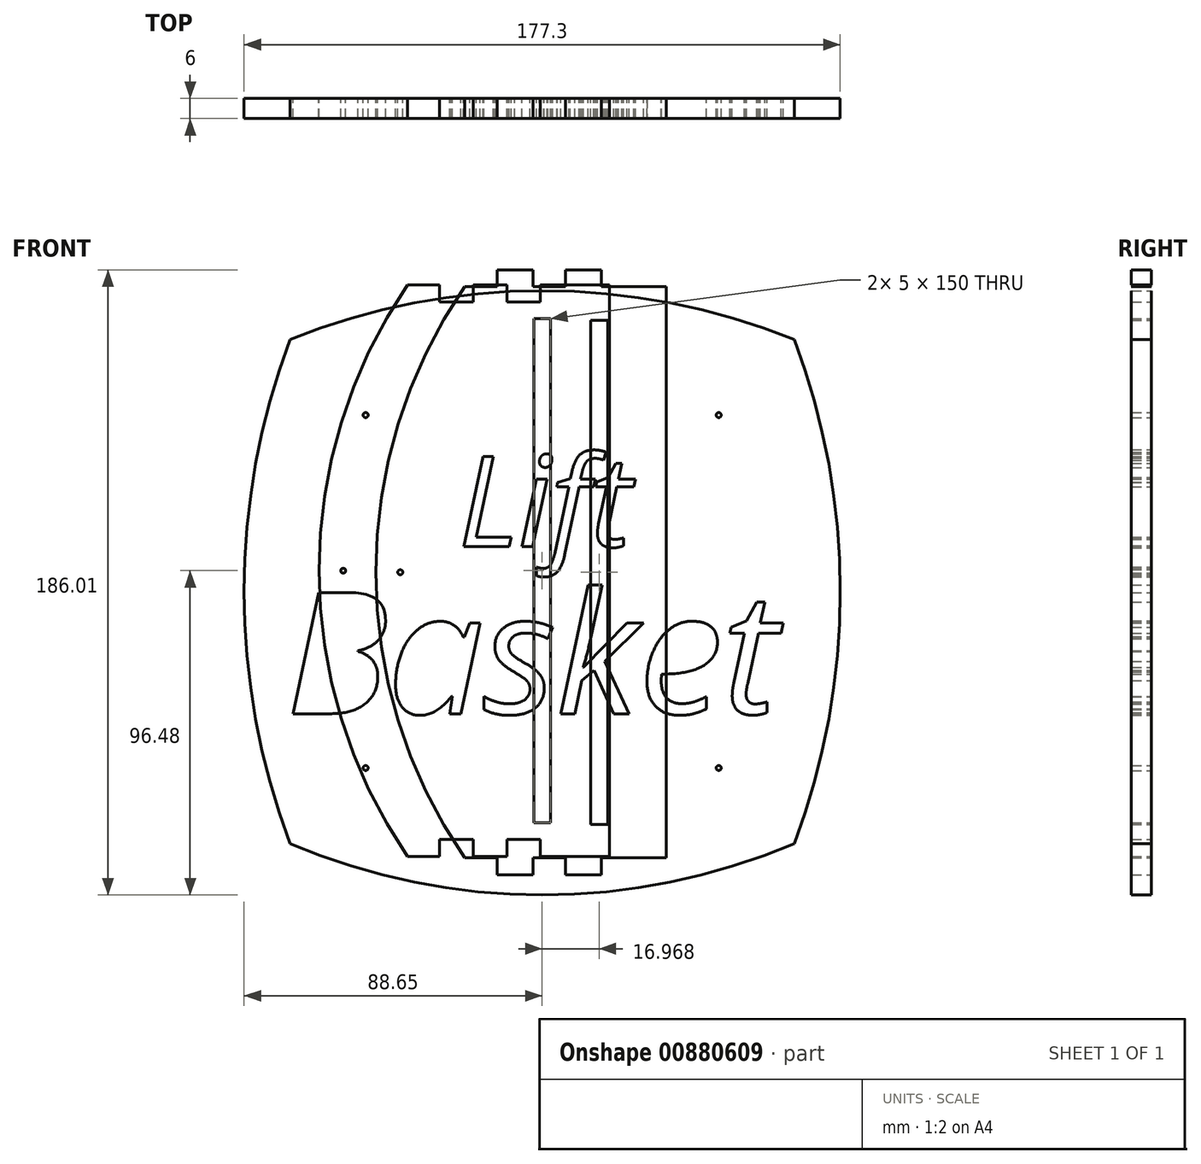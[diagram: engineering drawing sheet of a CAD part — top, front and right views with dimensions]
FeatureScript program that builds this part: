
annotation { "Feature Type Name" : "Feature", "Feature Type Description" : "" }
export const myFeature = defineFeature(function(context is Context, id is Id, definition is map)
    precondition{}
    {
        {
            var Q0;
            Q0=qCreatedBy(makeId("Front.planeOp"),FACE);
            var sketch = newSketch(context, id + "F0", { "sketchPlane" : qUnion([Q0])});
            skPoint(sketch, "E0.middle", {"position": v(0, 0) * mm});
            skPoint(sketch, "E1.start.orphan", {"position": v(-102.84, -173.45) * mm});
            skCircle(sketch, "E2", {"center": v(-52.5, -52.5) * mm, "radius": 0.75 * mm});
            skCircle(sketch, "E3", {"center": v(-52.5, 52.5) * mm, "radius": 0.75 * mm});
            skCircle(sketch, "E4", {"center": v(52.5, 52.5) * mm, "radius": 0.75 * mm});
            skCircle(sketch, "E5", {"center": v(52.5, -52.5) * mm, "radius": 0.75 * mm});
            skLineSegment(sketch, "E6", {"start": v(-75, 75) * mm, "end": v(-75, -75) * mm});
            skLineSegment(sketch, "E7", {"start": v(-75, 75) * mm, "end": v(75, 75) * mm});
            skLineSegment(sketch, "E8", {"start": v(75, 75) * mm, "end": v(75, -75) * mm});
            skLineSegment(sketch, "E9", {"start": v(-75, -75) * mm, "end": v(75, -75) * mm});
            skArc(sketch, "E10", {"start": v(75, -75) * mm, "mid": v(88.65, 0) * mm, "end": v(75, 75) * mm});
            skArc(sketch, "E11", {"start": v(-75, 75) * mm, "mid": v(-88.65, 0) * mm, "end": v(-75, -75) * mm});
            skText(sketch, "E12", { "text": "Basket", "fontName": "OpenSans-Italic.ttf"});
            skText(sketch, "E13", { "text": "Lift", "fontName": "OpenSans-Italic.ttf"});
            skArc(sketch, "E14", {"start": v(75, 75) * mm, "mid": v(0, 89.5) * mm, "end": v(-75, 75) * mm});
            skArc(sketch, "E15", {"start": v(-75, -75) * mm, "mid": v(0, -90.27) * mm, "end": v(75, -75) * mm});
            const initialGuessF0  = {"E12": [-0.0762, -0.03634, 1, 0, 0.03634], "E13": [-0.0249, 0.01335, 1, 0, 0.0271]};
            skSetInitialGuess(sketch, initialGuessF0);
            skSolve(sketch);
        }
        {
            var Q0;
            Q0=qCreatedBy(makeId("Front.planeOp"),FACE);
            var sketch = newSketch(context, id + "F1", { "sketchPlane" : qUnion([Q0])});
            skPoint(sketch, "E16.start.orphan", {"position": v(-103.07, -194.53) * mm});
            skLineSegment(sketch, "E17", {"start": v(20, 91.21) * mm, "end": v(-0.52, 91.21) * mm});
            skLineSegment(sketch, "E18", {"start": v(-40, 91.21) * mm, "end": v(-30.52, 91.21) * mm});
            skLineSegment(sketch, "E19", {"start": v(-20.52, 91.21) * mm, "end": v(-10.52, 91.21) * mm});
            skLineSegment(sketch, "E20.trimOffspring", {"start": v(-30.52, 91.21) * mm, "end": v(-40, 91.21) * mm});
            skLineSegment(sketch, "E21.trimOffspring", {"start": v(-10.52, 91.21) * mm, "end": v(-20.52, 91.21) * mm});
            skLineSegment(sketch, "E22", {"start": v(20, 91.21) * mm, "end": v(20, -78.79) * mm});
            skPoint(sketch, "E23", {"position": v(20, 6.21) * mm});
            skPoint(sketch, "E24.middle", {"position": v(0, 6.21) * mm});
            skPoint(sketch, "E24.cornerSnap0", {"position": v(10, 6.21) * mm});
            skLineSegment(sketch, "E25.bottom", {"start": v(2.5, -68.79) * mm, "end": v(-2.5, -68.79) * mm});
            skLineSegment(sketch, "E25.top", {"start": v(2.5, 81.21) * mm, "end": v(-2.5, 81.21) * mm});
            skLineSegment(sketch, "E25.left", {"start": v(2.5, -68.79) * mm, "end": v(2.5, 81.21) * mm});
            skLineSegment(sketch, "E25.right", {"start": v(-2.5, -68.79) * mm, "end": v(-2.5, 81.21) * mm});
            skArc(sketch, "E26", {"start": v(-40, 91.21) * mm, "mid": v(-66.4, 6.21) * mm, "end": v(-40, -78.79) * mm});
            skPoint(sketch, "E27", {"position": v(-59.17, 6.21) * mm});
            skCircle(sketch, "E28", {"center": v(-59.17, 6.21) * mm, "radius": 0.75 * mm});
            skLineSegment(sketch, "E29", {"start": v(-30.52, 91.21) * mm, "end": v(-30.52, 88.21) * mm});
            skLineSegment(sketch, "E30", {"start": v(-20.52, 88.21) * mm, "end": v(-20.52, 91.21) * mm});
            skLineSegment(sketch, "E31", {"start": v(-10.52, 91.21) * mm, "end": v(-10.52, 88.21) * mm});
            skLineSegment(sketch, "E32", {"start": v(-0.52, 88.21) * mm, "end": v(-0.52, 91.21) * mm});
            skLineSegment(sketch, "E33.MirrorCS", {"start": v(-0.52, -75.79) * mm, "end": v(-0.52, -78.79) * mm});
            skLineSegment(sketch, "E34.MirrorCS", {"start": v(-10.52, -78.79) * mm, "end": v(-10.52, -75.79) * mm});
            skLineSegment(sketch, "E35.MirrorCS", {"start": v(-20.52, -75.79) * mm, "end": v(-20.52, -78.79) * mm});
            skLineSegment(sketch, "E36.MirrorCS", {"start": v(-20.52, -78.79) * mm, "end": v(-10.52, -78.79) * mm});
            skLineSegment(sketch, "E37.MirrorCS", {"start": v(-30.52, -78.79) * mm, "end": v(-40, -78.79) * mm});
            skLineSegment(sketch, "E38.MirrorCS", {"start": v(20, -78.79) * mm, "end": v(-0.52, -78.79) * mm});
            skLineSegment(sketch, "E39.MirrorCS", {"start": v(-10.52, -78.79) * mm, "end": v(-20.52, -78.79) * mm});
            skPoint(sketch, "E40.orphan", {"position": v(-30.52, 86.21) * mm});
            skPoint(sketch, "E41.start.orphan", {"position": v(-10.52, 86.21) * mm});
            skPoint(sketch, "E42.orphan", {"position": v(-0.52, 86.21) * mm});
            skLineSegment(sketch, "E43", {"start": v(-30.52, -78.79) * mm, "end": v(-30.52, -75.79) * mm});
            skLineSegment(sketch, "E44", {"start": v(-30.52, 86.21) * mm, "end": v(-30.52, 88.21) * mm});
            skLineSegment(sketch, "E45", {"start": v(-30.52, 86.21) * mm, "end": v(-20.52, 86.21) * mm});
            skLineSegment(sketch, "E46", {"start": v(-20.52, 86.21) * mm, "end": v(-20.52, 88.21) * mm});
            skLineSegment(sketch, "E47", {"start": v(-10.52, 86.21) * mm, "end": v(-10.52, 88.21) * mm});
            skLineSegment(sketch, "E48", {"start": v(-0.52, 88.21) * mm, "end": v(-0.52, 86.21) * mm});
            skLineSegment(sketch, "E49", {"start": v(-0.52, 86.21) * mm, "end": v(-10.52, 86.21) * mm});
            skLineSegment(sketch, "E50", {"start": v(-30.52, -75.79) * mm, "end": v(-30.52, -73.79) * mm});
            skLineSegment(sketch, "E51", {"start": v(-30.52, -73.79) * mm, "end": v(-20.52, -73.79) * mm});
            skLineSegment(sketch, "E52", {"start": v(-20.52, -73.79) * mm, "end": v(-20.52, -75.79) * mm});
            skLineSegment(sketch, "E53", {"start": v(-10.52, -75.79) * mm, "end": v(-10.52, -73.79) * mm});
            skLineSegment(sketch, "E54", {"start": v(-10.52, -73.79) * mm, "end": v(-0.52, -73.79) * mm});
            skLineSegment(sketch, "E55", {"start": v(-0.52, -73.79) * mm, "end": v(-0.52, -75.79) * mm});
            skSolve(sketch);
        }
        {
            var Q0;
            Q0=qCreatedBy(makeId("Front.planeOp"),FACE);
            var sketch = newSketch(context, id + "F2", { "sketchPlane" : qUnion([Q0])});
            skPoint(sketch, "E56.start.orphan", {"position": v(-17.96, -180.43) * mm});
            skPoint(sketch, "E57.start.orphan", {"position": v(-86.1, -195) * mm});
            skLineSegment(sketch, "E58", {"start": v(36.97, 90.74) * mm, "end": v(36.97, -79.26) * mm});
            skPoint(sketch, "E59", {"position": v(36.97, 5.74) * mm});
            skPoint(sketch, "E60.middle", {"position": v(16.97, 5.74) * mm});
            skPoint(sketch, "E60.cornerSnap0", {"position": v(26.97, 5.74) * mm});
            skLineSegment(sketch, "E61.bottom", {"start": v(19.47, -69.26) * mm, "end": v(14.47, -69.26) * mm});
            skLineSegment(sketch, "E61.top", {"start": v(19.47, 80.74) * mm, "end": v(14.47, 80.74) * mm});
            skLineSegment(sketch, "E61.left", {"start": v(19.47, -69.26) * mm, "end": v(19.47, 80.74) * mm});
            skLineSegment(sketch, "E61.right", {"start": v(14.47, -69.26) * mm, "end": v(14.47, 80.74) * mm});
            skArc(sketch, "E62", {"start": v(-23.03, 90.74) * mm, "mid": v(-49.44, 5.74) * mm, "end": v(-23.03, -79.26) * mm});
            skPoint(sketch, "E63", {"position": v(-42.2, 5.74) * mm});
            skCircle(sketch, "E64", {"center": v(-42.2, 5.74) * mm, "radius": 0.75 * mm});
            skLineSegment(sketch, "E65", {"start": v(-23.03, -79.26) * mm, "end": v(-13.33, -79.26) * mm});
            skLineSegment(sketch, "E66", {"start": v(-13.33, -79.26) * mm, "end": v(-13.33, -82.26) * mm});
            skLineSegment(sketch, "E67", {"start": v(-2.73, -82.26) * mm, "end": v(-2.73, -79.26) * mm});
            skLineSegment(sketch, "E68", {"start": v(-2.73, -79.26) * mm, "end": v(6.97, -79.26) * mm});
            skLineSegment(sketch, "E69", {"start": v(6.97, -79.26) * mm, "end": v(6.97, -82.26) * mm});
            skLineSegment(sketch, "E70", {"start": v(17.57, -82.26) * mm, "end": v(17.57, -79.26) * mm});
            skLineSegment(sketch, "E71", {"start": v(17.57, -79.26) * mm, "end": v(36.97, -79.26) * mm});
            skLineSegment(sketch, "E72.MirrorCS", {"start": v(17.57, 93.74) * mm, "end": v(17.57, 90.74) * mm});
            skLineSegment(sketch, "E73.MirrorCS", {"start": v(-13.33, 90.74) * mm, "end": v(-13.33, 93.74) * mm});
            skLineSegment(sketch, "E74.MirrorCS", {"start": v(-2.73, 93.74) * mm, "end": v(-2.73, 90.74) * mm});
            skLineSegment(sketch, "E75.MirrorCS", {"start": v(6.97, 90.74) * mm, "end": v(6.97, 93.74) * mm});
            skLineSegment(sketch, "E76.MirrorCS", {"start": v(-2.73, 90.74) * mm, "end": v(6.97, 90.74) * mm});
            skLineSegment(sketch, "E77.MirrorCS", {"start": v(17.57, 90.74) * mm, "end": v(36.97, 90.74) * mm});
            skLineSegment(sketch, "E78.MirrorCS", {"start": v(-23.03, 90.74) * mm, "end": v(-13.33, 90.74) * mm});
            skPoint(sketch, "E79.start.orphan", {"position": v(-13.33, -84.26) * mm});
            skPoint(sketch, "E80.start.orphan", {"position": v(6.97, -84.26) * mm});
            skLineSegment(sketch, "E81", {"start": v(-13.33, 93.74) * mm, "end": v(-13.33, 95.74) * mm});
            skLineSegment(sketch, "E82", {"start": v(-13.33, 95.74) * mm, "end": v(-2.73, 95.74) * mm});
            skLineSegment(sketch, "E83", {"start": v(-2.73, 95.74) * mm, "end": v(-2.73, 93.74) * mm});
            skLineSegment(sketch, "E84", {"start": v(6.97, 95.74) * mm, "end": v(17.57, 95.74) * mm});
            skLineSegment(sketch, "E85", {"start": v(6.97, 93.74) * mm, "end": v(6.97, 95.74) * mm});
            skLineSegment(sketch, "E86", {"start": v(17.57, 93.74) * mm, "end": v(17.57, 95.74) * mm});
            skLineSegment(sketch, "E87", {"start": v(-13.33, -84.26) * mm, "end": v(-13.33, -82.26) * mm});
            skLineSegment(sketch, "E88", {"start": v(-13.33, -84.26) * mm, "end": v(-2.73, -84.26) * mm});
            skLineSegment(sketch, "E89", {"start": v(-2.73, -84.26) * mm, "end": v(-2.73, -82.26) * mm});
            skLineSegment(sketch, "E90", {"start": v(6.97, -84.26) * mm, "end": v(6.97, -82.26) * mm});
            skLineSegment(sketch, "E91", {"start": v(6.97, -84.26) * mm, "end": v(17.57, -84.26) * mm});
            skLineSegment(sketch, "E92", {"start": v(17.57, -84.26) * mm, "end": v(17.57, -82.26) * mm});
            skSolve(sketch);
        }
        {
            var Q0;
            Q0 = qSketchRegion(id + "F0", true);
            extrude(context, id + "F3", {"entities" : qUnion([Q0]), "depth" : 6 * mm, "offsetDistance" : 25 * mm});
        }
        {
            var Q0;
            Q0 = qSketchRegion(id + "F1", true);
            extrude(context, id + "F4", {"entities" : qUnion([Q0]), "depth" : 6 * mm, "offsetDistance" : 25 * mm});
        }
        {
            var Q0;
            Q0 = qSketchRegion(id + "F2", true);
            extrude(context, id + "F5", {"entities" : qUnion([Q0]), "depth" : 6 * mm, "offsetDistance" : 25 * mm});
        }
    });
